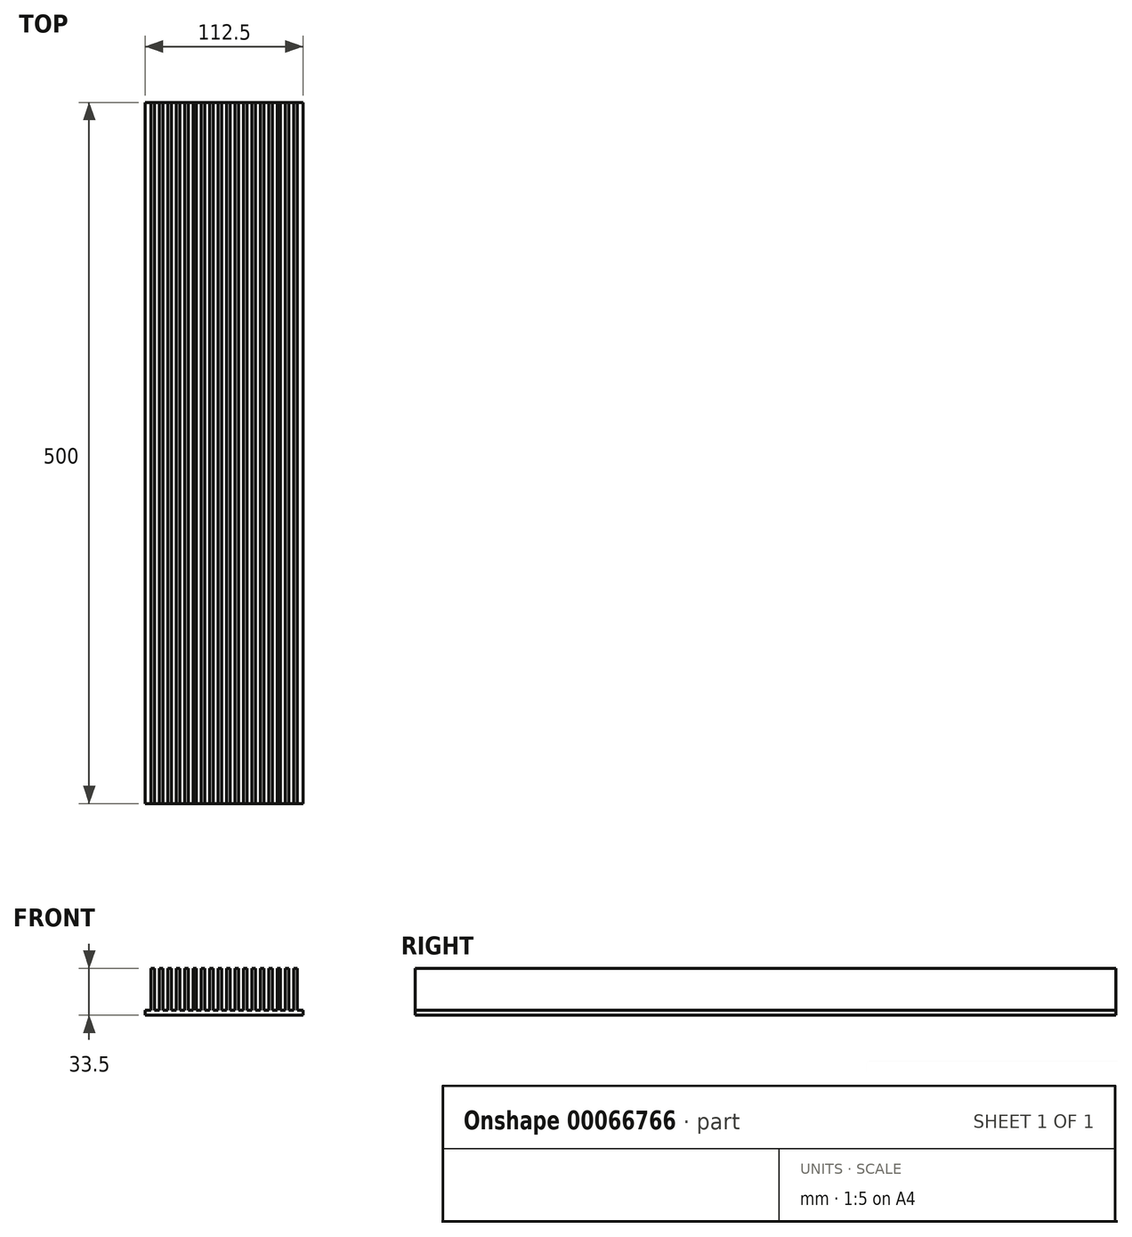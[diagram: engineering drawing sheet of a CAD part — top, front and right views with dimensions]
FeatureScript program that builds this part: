
annotation { "Feature Type Name" : "Feature", "Feature Type Description" : "" }
export const myFeature = defineFeature(function(context is Context, id is Id, definition is map)
    precondition{}
    {
        {
            var Q0;
            Q0=qCreatedBy(makeId("Front.planeOp"),FACE);
            var sketch = newSketch(context, id + "F0", { "sketchPlane" : qUnion([Q0])});
            skLineSegment(sketch, "E0", {"start": v(0, 0) * mm, "end": v(56.25, 0) * mm});
            skLineSegment(sketch, "E1", {"start": v(56.25, 0) * mm, "end": v(56.25, 3.5) * mm});
            skLineSegment(sketch, "E2", {"start": v(56.25, 3.5) * mm, "end": v(52.25, 3.5) * mm});
            skLineSegment(sketch, "E3", {"start": v(52.25, 3.5) * mm, "end": v(52.25, 33.5) * mm});
            skLineSegment(sketch, "E4", {"start": v(52.25, 33.5) * mm, "end": v(49.75, 33.5) * mm});
            skLineSegment(sketch, "E5", {"start": v(49.75, 33.5) * mm, "end": v(49.75, 3.5) * mm});
            skLineSegment(sketch, "E6", {"start": v(0, 0) * mm, "end": v(-56.25, 0) * mm});
            skLineSegment(sketch, "E7", {"start": v(-56.25, 0) * mm, "end": v(-56.25, 3.5) * mm});
            skLineSegment(sketch, "E8", {"start": v(-56.25, 3.5) * mm, "end": v(-52.25, 3.5) * mm});
            skLineSegment(sketch, "E9", {"start": v(-52.25, 3.5) * mm, "end": v(-52.25, 55.1) * mm, "construction": true});
            skLineSegment(sketch, "E10", {"start": v(-52.25, 3.5) * mm, "end": v(49.75, 3.5) * mm});
            skLineSegment(sketch, "E11.1.0.0", {"start": v(46.25, 33.5) * mm, "end": v(43.75, 33.5) * mm});
            skLineSegment(sketch, "E11.1.0.1", {"start": v(46.25, 3.5) * mm, "end": v(46.25, 33.5) * mm});
            skLineSegment(sketch, "E11.1.0.2", {"start": v(43.75, 33.5) * mm, "end": v(43.75, 3.5) * mm});
            skLineSegment(sketch, "E11.2.0.0", {"start": v(40.25, 33.5) * mm, "end": v(37.75, 33.5) * mm});
            skLineSegment(sketch, "E11.2.0.1", {"start": v(40.25, 3.5) * mm, "end": v(40.25, 33.5) * mm});
            skLineSegment(sketch, "E11.2.0.2", {"start": v(37.75, 33.5) * mm, "end": v(37.75, 3.5) * mm});
            skLineSegment(sketch, "E11.3.0.0", {"start": v(34.25, 33.5) * mm, "end": v(31.75, 33.5) * mm});
            skLineSegment(sketch, "E11.3.0.1", {"start": v(34.25, 3.5) * mm, "end": v(34.25, 33.5) * mm});
            skLineSegment(sketch, "E11.3.0.2", {"start": v(31.75, 33.5) * mm, "end": v(31.75, 3.5) * mm});
            skLineSegment(sketch, "E11.4.0.0", {"start": v(28.25, 33.5) * mm, "end": v(25.75, 33.5) * mm});
            skLineSegment(sketch, "E11.4.0.1", {"start": v(28.25, 3.5) * mm, "end": v(28.25, 33.5) * mm});
            skLineSegment(sketch, "E11.4.0.2", {"start": v(25.75, 33.5) * mm, "end": v(25.75, 3.5) * mm});
            skLineSegment(sketch, "E11.5.0.0", {"start": v(22.25, 33.5) * mm, "end": v(19.75, 33.5) * mm});
            skLineSegment(sketch, "E11.5.0.1", {"start": v(22.25, 3.5) * mm, "end": v(22.25, 33.5) * mm});
            skLineSegment(sketch, "E11.5.0.2", {"start": v(19.75, 33.5) * mm, "end": v(19.75, 3.5) * mm});
            skLineSegment(sketch, "E11.6.0.0", {"start": v(16.25, 33.5) * mm, "end": v(13.75, 33.5) * mm});
            skLineSegment(sketch, "E11.6.0.1", {"start": v(16.25, 3.5) * mm, "end": v(16.25, 33.5) * mm});
            skLineSegment(sketch, "E11.6.0.2", {"start": v(13.75, 33.5) * mm, "end": v(13.75, 3.5) * mm});
            skLineSegment(sketch, "E11.7.0.0", {"start": v(10.25, 33.5) * mm, "end": v(7.75, 33.5) * mm});
            skLineSegment(sketch, "E11.7.0.1", {"start": v(10.25, 3.5) * mm, "end": v(10.25, 33.5) * mm});
            skLineSegment(sketch, "E11.7.0.2", {"start": v(7.75, 33.5) * mm, "end": v(7.75, 3.5) * mm});
            skLineSegment(sketch, "E11.8.0.0", {"start": v(4.25, 33.5) * mm, "end": v(1.75, 33.5) * mm});
            skLineSegment(sketch, "E11.8.0.1", {"start": v(4.25, 3.5) * mm, "end": v(4.25, 33.5) * mm});
            skLineSegment(sketch, "E11.8.0.2", {"start": v(1.75, 33.5) * mm, "end": v(1.75, 3.5) * mm});
            skLineSegment(sketch, "E11.9.0.0", {"start": v(-1.75, 33.5) * mm, "end": v(-4.25, 33.5) * mm});
            skLineSegment(sketch, "E11.9.0.1", {"start": v(-1.75, 3.5) * mm, "end": v(-1.75, 33.5) * mm});
            skLineSegment(sketch, "E11.9.0.2", {"start": v(-4.25, 33.5) * mm, "end": v(-4.25, 3.5) * mm});
            skLineSegment(sketch, "E11.10.0.0", {"start": v(-7.75, 33.5) * mm, "end": v(-10.25, 33.5) * mm});
            skLineSegment(sketch, "E11.10.0.1", {"start": v(-7.75, 3.5) * mm, "end": v(-7.75, 33.5) * mm});
            skLineSegment(sketch, "E11.10.0.2", {"start": v(-10.25, 33.5) * mm, "end": v(-10.25, 3.5) * mm});
            skLineSegment(sketch, "E11.11.0.0", {"start": v(-13.75, 33.5) * mm, "end": v(-16.25, 33.5) * mm});
            skLineSegment(sketch, "E11.11.0.1", {"start": v(-13.75, 3.5) * mm, "end": v(-13.75, 33.5) * mm});
            skLineSegment(sketch, "E11.11.0.2", {"start": v(-16.25, 33.5) * mm, "end": v(-16.25, 3.5) * mm});
            skLineSegment(sketch, "E11.12.0.0", {"start": v(-19.75, 33.5) * mm, "end": v(-22.25, 33.5) * mm});
            skLineSegment(sketch, "E11.12.0.1", {"start": v(-19.75, 3.5) * mm, "end": v(-19.75, 33.5) * mm});
            skLineSegment(sketch, "E11.12.0.2", {"start": v(-22.25, 33.5) * mm, "end": v(-22.25, 3.5) * mm});
            skLineSegment(sketch, "E11.13.0.0", {"start": v(-25.75, 33.5) * mm, "end": v(-28.25, 33.5) * mm});
            skLineSegment(sketch, "E11.13.0.1", {"start": v(-25.75, 3.5) * mm, "end": v(-25.75, 33.5) * mm});
            skLineSegment(sketch, "E11.13.0.2", {"start": v(-28.25, 33.5) * mm, "end": v(-28.25, 3.5) * mm});
            skLineSegment(sketch, "E11.14.0.0", {"start": v(-31.75, 33.5) * mm, "end": v(-34.25, 33.5) * mm});
            skLineSegment(sketch, "E11.14.0.1", {"start": v(-31.75, 3.5) * mm, "end": v(-31.75, 33.5) * mm});
            skLineSegment(sketch, "E11.14.0.2", {"start": v(-34.25, 33.5) * mm, "end": v(-34.25, 3.5) * mm});
            skLineSegment(sketch, "E11.15.0.0", {"start": v(-37.75, 33.5) * mm, "end": v(-40.25, 33.5) * mm});
            skLineSegment(sketch, "E11.15.0.1", {"start": v(-37.75, 3.5) * mm, "end": v(-37.75, 33.5) * mm});
            skLineSegment(sketch, "E11.15.0.2", {"start": v(-40.25, 33.5) * mm, "end": v(-40.25, 3.5) * mm});
            skLineSegment(sketch, "E11.16.0.0", {"start": v(-43.75, 33.5) * mm, "end": v(-46.25, 33.5) * mm});
            skLineSegment(sketch, "E11.16.0.1", {"start": v(-43.75, 3.5) * mm, "end": v(-43.75, 33.5) * mm});
            skLineSegment(sketch, "E11.16.0.2", {"start": v(-46.25, 33.5) * mm, "end": v(-46.25, 3.5) * mm});
            skLineSegment(sketch, "E11.17.0.0", {"start": v(-49.75, 33.5) * mm, "end": v(-52.25, 33.5) * mm});
            skLineSegment(sketch, "E11.17.0.1", {"start": v(-49.75, 3.5) * mm, "end": v(-49.75, 33.5) * mm});
            skLineSegment(sketch, "E11.17.0.2", {"start": v(-52.25, 33.5) * mm, "end": v(-52.25, 3.5) * mm});
            skLineSegment(sketch, "E11.direction1", {"start": v(49.75, 33.5) * mm, "end": v(43.75, 33.5) * mm, "construction": true});
            skSolve(sketch);
        }
        {
            var Q0;
            Q0=qSketchRegion(id+"F0",true);
            extrude(context, id + "F1", {"entities" : qUnion([Q0]), "depth" : 500 * mm});
        }
    });
